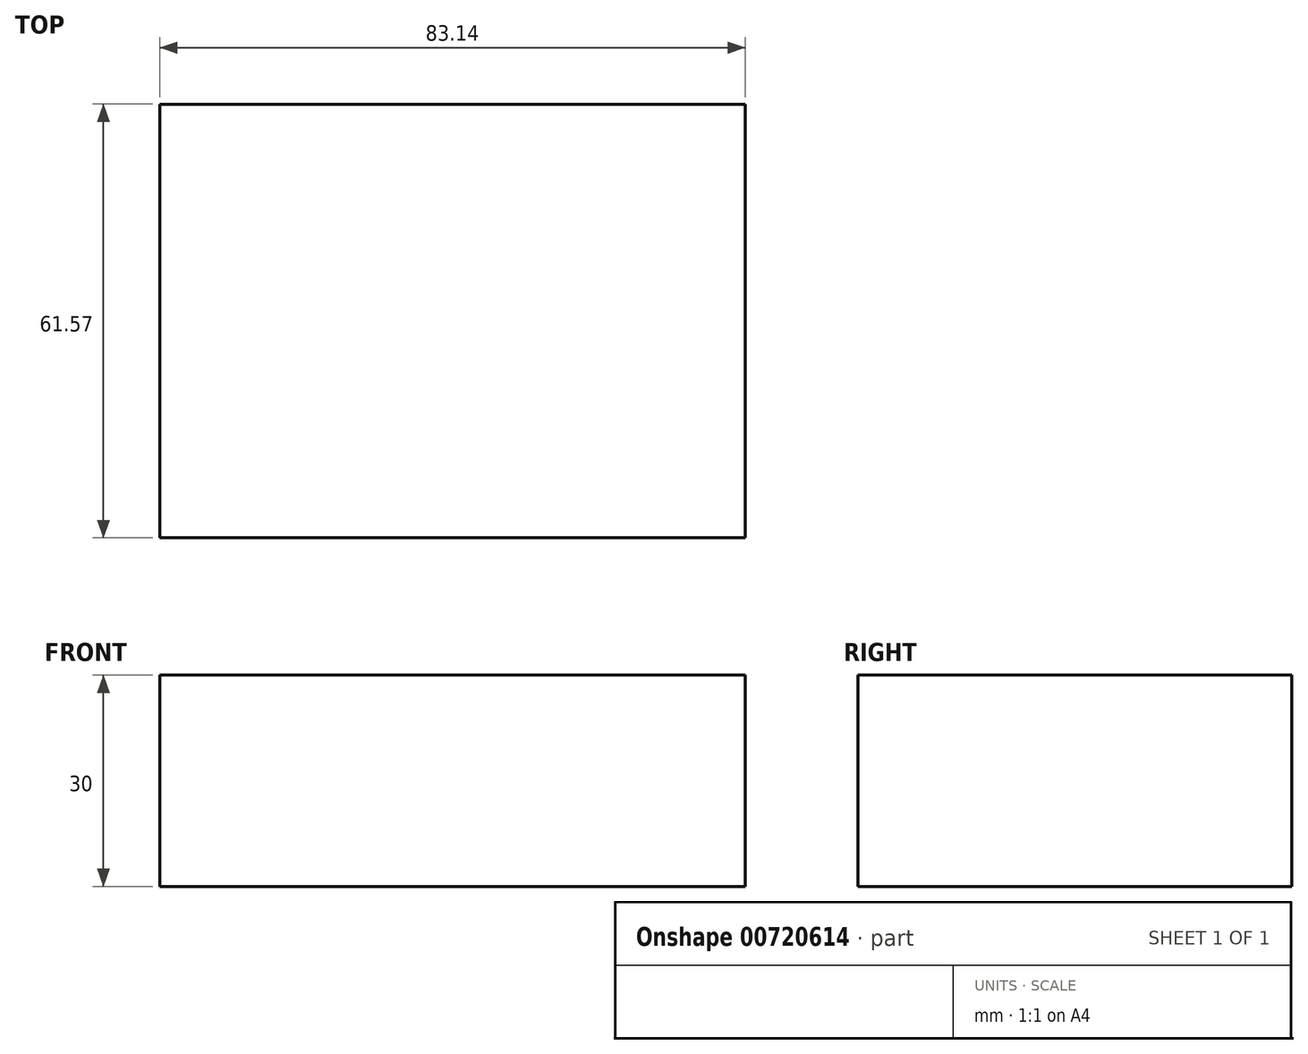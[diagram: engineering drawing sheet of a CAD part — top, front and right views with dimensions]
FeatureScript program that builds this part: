
annotation { "Feature Type Name" : "Feature", "Feature Type Description" : "" }
export const myFeature = defineFeature(function(context is Context, id is Id, definition is map)
    precondition{}
    {
        {
            var Q0;
            Q0=qCreatedBy(makeId("Top.planeOp"),FACE);
            var sketch = newSketch(context, id + "F0", { "sketchPlane" : qUnion([Q0])});
            skLineSegment(sketch, "E0.bottom", {"start": v(-117.42, -25.4) * mm, "end": v(-34.28, -25.4) * mm});
            skLineSegment(sketch, "E0.top", {"start": v(-117.42, 36.17) * mm, "end": v(-34.28, 36.17) * mm});
            skLineSegment(sketch, "E0.left", {"start": v(-117.42, -25.4) * mm, "end": v(-117.42, 36.17) * mm});
            skLineSegment(sketch, "E0.right", {"start": v(-34.28, -25.4) * mm, "end": v(-34.28, 36.17) * mm});
            skLineSegment(sketch, "E1.bottom", {"start": v(-117.42, 0) * mm, "end": v(-117.42, 0) * mm});
            skLineSegment(sketch, "E1.top", {"start": v(-117.42, -25.4) * mm, "end": v(-117.42, -25.4) * mm});
            skLineSegment(sketch, "E1.left", {"start": v(-117.42, 0) * mm, "end": v(-117.42, -25.4) * mm});
            skLineSegment(sketch, "E1.right", {"start": v(-117.42, 0) * mm, "end": v(-117.42, -25.4) * mm});
            skSolve(sketch);
        }
        {
            var Q0;
            Q0=makeQuery(id+"F0.imprint","IMPRINT",FACE,{"disambiguationData":[TD([[makeQuery(id+"F0.imprint","IMPRINT",EDGE,{"derivedFrom":sQuery(id+"F0.wireOp",EDGE,"E0.bottom")}),1.0]])]});
            extrude(context, id + "F1", {"entities" : qUnion([Q0]), "depth" : 25 * mm, "offsetDistance" : 25 * mm});
        }
        {
            var Q0;
            Q0=makeQuery(id+"F1.opExtrude","CAP_FACE",FACE,{"disambiguationData":[OSD([sQuery(id+"F0.wireOp",EDGE,"E0.bottom"),sQuery(id+"F0.wireOp",EDGE,"E0.top"),sQuery(id+"F0.wireOp",EDGE,"E0.left"),sQuery(id+"F0.wireOp",EDGE,"E0.right"),sQuery(id+"F0.wireOp",EDGE,"E1.right")])],"isStart":true});
            var sketch = newSketch(context, id + "F2", { "sketchPlane" : qUnion([Q0])});
            skSolve(sketch);
        }
        {
            var Q0;
            Q0 = qSketchRegion(id + "F2", true);
            var Q1;
            Q1=makeQuery(id+"F2.imprint","IMPRINT",FACE,{"disambiguationData":[TD([[makeQuery(id+"F2.imprint","IMPRINT",EDGE,{"derivedFrom":makeQuery(id+"F1.opExtrude","CAP_EDGE",EDGE,{"disambiguationData":[OSD([sQuery(id+"F0.wireOp",EDGE,"E0.bottom")])],"isStart":true})}),-1.0]])]});
            extrude(context, id + "F3", {"entities" : qUnion([Q0, Q1]), "operationType" : NewBodyOperationType.ADD, "depth" : 5 * mm, "offsetDistance" : 25 * mm});
        }
    });
